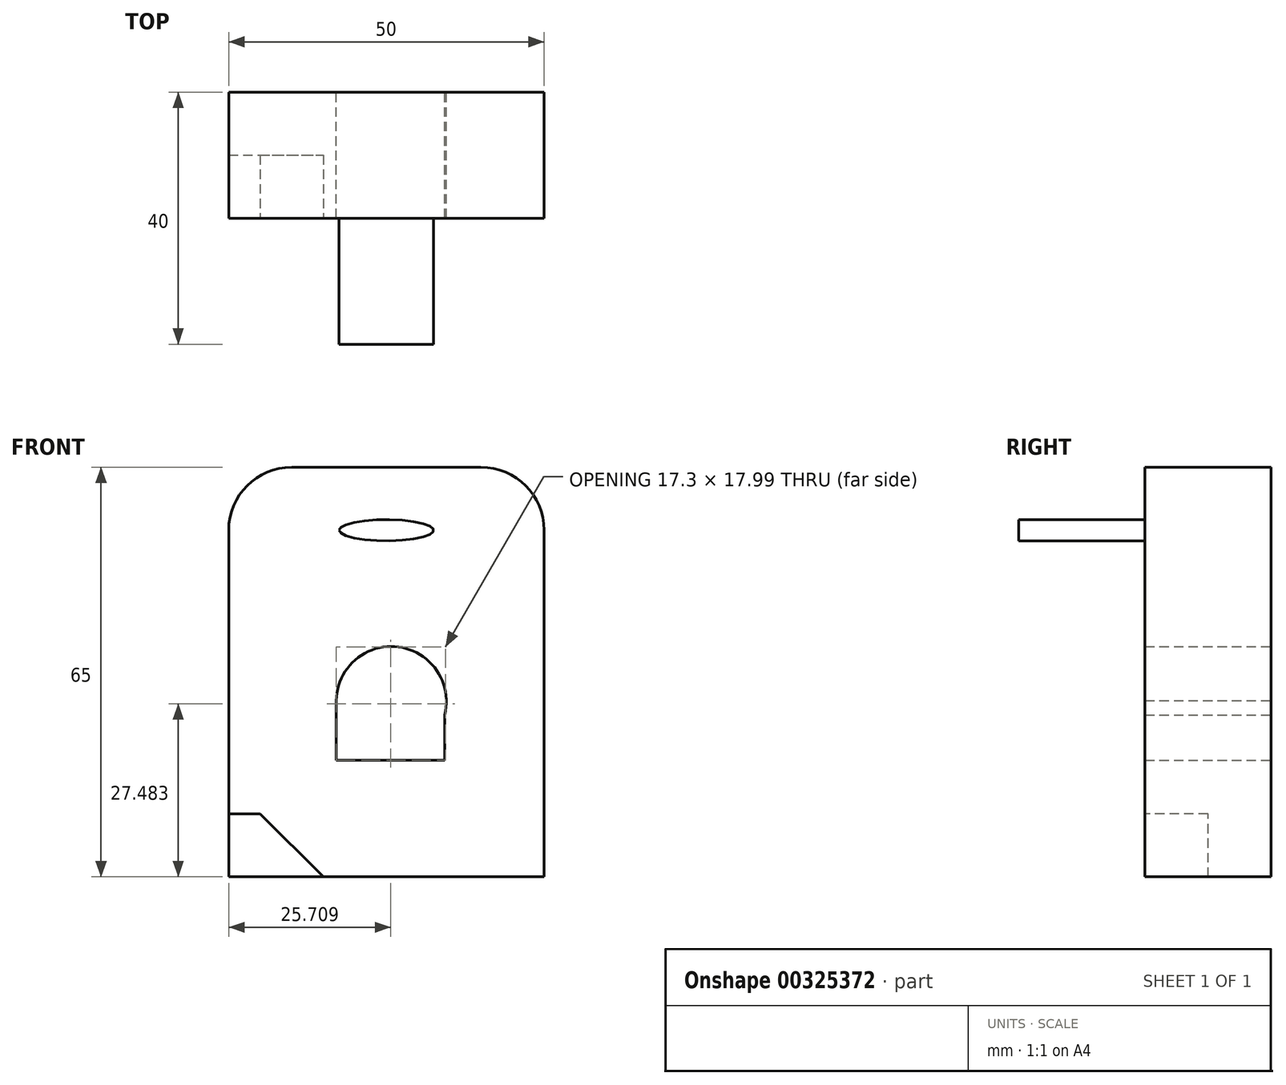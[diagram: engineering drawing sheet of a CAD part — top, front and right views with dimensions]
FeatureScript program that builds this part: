
annotation { "Feature Type Name" : "Feature", "Feature Type Description" : "" }
export const myFeature = defineFeature(function(context is Context, id is Id, definition is map)
    precondition{}
    {
        {
            var Q0;
            Q0=qCreatedBy(makeId("Front.planeOp"),FACE);
            var sketch = newSketch(context, id + "F0", { "sketchPlane" : qUnion([Q0])});
            skLineSegment(sketch, "E0.bottom", {"start": v(-25, -32.5) * mm, "end": v(25, -32.5) * mm});
            skLineSegment(sketch, "E0.top", {"start": v(-25, 32.5) * mm, "end": v(25, 32.5) * mm});
            skLineSegment(sketch, "E0.left", {"start": v(-25, -32.5) * mm, "end": v(-25, 32.5) * mm});
            skLineSegment(sketch, "E0.right", {"start": v(25, -32.5) * mm, "end": v(25, 32.5) * mm});
            skPoint(sketch, "E0.middle", {"position": v(0, 0) * mm});
            skSolve(sketch);
        }
        {
            var Q0;
            Q0=makeQuery(id+"F0.imprint","IMPRINT",FACE,{"disambiguationData":[TD([[makeQuery(id+"F0.imprint","IMPRINT",EDGE,{"derivedFrom":sQuery(id+"F0.wireOp",EDGE,"E0.bottom")}),1.0]])]});
            extrude(context, id + "F1", {"entities" : qUnion([Q0]), "depth" : 20 * mm});
        }
        {
            var Q0;
            Q0=makeQuery(id+"F1.opExtrude","CAP_FACE",FACE,{"disambiguationData":[OSD([sQuery(id+"F0.wireOp",EDGE,"E0.bottom"),sQuery(id+"F0.wireOp",EDGE,"E0.top"),sQuery(id+"F0.wireOp",EDGE,"E0.left"),sQuery(id+"F0.wireOp",EDGE,"E0.right")])],"isStart":false});
            var sketch = newSketch(context, id + "F2", { "sketchPlane" : qUnion([Q0])});
            skLineSegment(sketch, "E1", {"start": v(9.23, -14.01) * mm, "end": v(-7.94, -14.01) * mm});
            skLineSegment(sketch, "E2", {"start": v(-7.94, -14.01) * mm, "end": v(-7.94, -4.56) * mm});
            skLineSegment(sketch, "E3", {"start": v(-7.94, -4.56) * mm, "end": v(9.23, -4.56) * mm});
            skLineSegment(sketch, "E4", {"start": v(9.23, -4.56) * mm, "end": v(9.23, -14.01) * mm});
            skCircle(sketch, "E5", {"center": v(0.78, -4.67) * mm, "radius": 8.72 * mm});
            skCircle(sketch, "E6", {"center": v(-8.67, -44.04) * mm, "radius": 6.44 * mm, "construction": true});
            skSolve(sketch);
        }
        {
            var Q0;
            {var subQ0=sQuery(id+"F2.wireOp",EDGE,"E1");Q0=makeQuery(id+"F2.imprint","IMPRINT",FACE,{"disambiguationData":[TD([[makeQuery(id+"F2.imprint","IMPRINT",EDGE,{"derivedFrom":subQ0}),-1.0]])]});}
            var Q1;
            {var subQ0=sQuery(id+"F2.wireOp",EDGE,"E3");Q1=makeQuery(id+"F2.imprint","IMPRINT",FACE,{"disambiguationData":[TD([[makeQuery(id+"F2.imprint","IMPRINT",EDGE,{"derivedFrom":subQ0}),1.0]])]});}
            var Q2;
            {var subQ1=sQuery(id+"F2.wireOp",EDGE,"E3");Q2=makeQuery(id+"F2.imprint","IMPRINT",FACE,{"disambiguationData":[TD([[makeQuery(id+"F2.imprint","IMPRINT",EDGE,{"derivedFrom":subQ1}),-1.0]])]});}
            extrude(context, id + "F3", {"entities" : qUnion([Q0, Q1, Q2]), "operationType" : NewBodyOperationType.REMOVE, "depth" : 25.4 * mm, "hasSecondDirection" : true, "secondDirectionOppositeDirection" : true, "secondDirectionDepth" : 25.4 * mm});
        }
        {
            var Q0;
            Q0=makeQuery(id+"F1.opExtrude","SWEPT_EDGE",EDGE,{"disambiguationData":[OSD([sQuery(id+"F0.wireOp",EDGE,"E0.top"),sQuery(id+"F0.wireOp",EDGE,"E0.right")])]});
            var Q1;
            Q1=makeQuery(id+"F1.opExtrude","SWEPT_EDGE",EDGE,{"disambiguationData":[OSD([sQuery(id+"F0.wireOp",EDGE,"E0.top"),sQuery(id+"F0.wireOp",EDGE,"E0.left")])]});
            fillet(context, id + "F4", {"entities" : qUnion([Q0, Q1]), "radius" : 10 * mm, "tangentPropagation" : true, "allowEdgeOverflow" : false});
        }
        {
            var Q0;
            Q0=makeQuery(id+"F1.opExtrude","CAP_FACE",FACE,{"disambiguationData":[OSD([sQuery(id+"F0.wireOp",EDGE,"E0.bottom"),sQuery(id+"F0.wireOp",EDGE,"E0.top"),sQuery(id+"F0.wireOp",EDGE,"E0.left"),sQuery(id+"F0.wireOp",EDGE,"E0.right")])],"isStart":false});
            var sketch = newSketch(context, id + "F5", { "sketchPlane" : qUnion([Q0])});
            skLineSegment(sketch, "E7", {"start": v(-25, -22.5) * mm, "end": v(-20, -22.5) * mm});
            skLineSegment(sketch, "E8", {"start": v(-20, -22.5) * mm, "end": v(-10, -32.5) * mm});
            skLineSegment(sketch, "E9", {"start": v(-10, -32.5) * mm, "end": v(-25, -32.5) * mm});
            skLineSegment(sketch, "E10", {"start": v(-25, -32.5) * mm, "end": v(-25, -22.5) * mm});
            skSolve(sketch);
        }
        {
            var Q0;
            Q0=makeQuery(id+"F5.imprint","IMPRINT",FACE,{"disambiguationData":[TD([[makeQuery(id+"F5.imprint","IMPRINT",EDGE,{"derivedFrom":sQuery(id+"F5.wireOp",EDGE,"E7")}),-1.0]])]});
            extrude(context, id + "F6", {"entities" : qUnion([Q0]), "operationType" : NewBodyOperationType.REMOVE, "oppositeDirection" : true, "depth" : 10 * mm});
        }
        {
            var Q0;
            Q0=makeQuery(id+"F1.opExtrude","CAP_FACE",FACE,{"disambiguationData":[OSD([sQuery(id+"F0.wireOp",EDGE,"E0.bottom"),sQuery(id+"F0.wireOp",EDGE,"E0.top"),sQuery(id+"F0.wireOp",EDGE,"E0.left"),sQuery(id+"F0.wireOp",EDGE,"E0.right")])],"isStart":false});
            var sketch = newSketch(context, id + "F7", { "sketchPlane" : qUnion([Q0])});
            skEllipse(sketch, "E11", {"center": v(0, 22.5) * mm, "majorRadius": 7.5 * mm, "minorRadius": 1.68 * mm, "majorAxis": v(-1, 0)});
            skSolve(sketch);
        }
        {
            var Q0;
            Q0=makeQuery(id+"F7.imprint","IMPRINT",FACE,{"disambiguationData":[TD([[makeQuery(id+"F7.imprint","IMPRINT",EDGE,{"derivedFrom":sQuery(id+"F7.wireOp",EDGE,"E11")}),1.0]])]});
            extrude(context, id + "F8", {"entities" : qUnion([Q0]), "operationType" : NewBodyOperationType.ADD, "depth" : 20 * mm});
        }
        {
            var Q0;
            Q0=makeQuery(id+"F1.opExtrude","SWEPT_FACE",FACE,{"disambiguationData":[OSD([sQuery(id+"F0.wireOp",EDGE,"E0.bottom")])]});
            var sketch = newSketch(context, id + "F9", { "sketchPlane" : qUnion([Q0])});
            skCircle(sketch, "E12", {"center": v(25, 20) * mm, "radius": 5 * mm});
            skSolve(sketch);
        }
        {
            var Q0;
            {var subQ0=sQuery(id+"F9.wireOp",EDGE,"E12");var subQ1=sQuery(id+"F0.wireOp",EDGE,"E0.bottom");var subQ4=makeQuery(id+"F1.opExtrude","CAP_EDGE",EDGE,{"disambiguationData":[OSD([subQ1])],"isStart":false});var subQ5=makeQuery(id+"F9.imprint","INTERSECT",VERTEX,{"derivedFrom":[subQ4,subQ0]});Q0=makeQuery(id+"F9.imprint","IMPRINT",FACE,{"disambiguationData":[TD([[makeQuery(id+"F9.imprint","IMPRINT",EDGE,{"disambiguationData":[TD([[subQ5,1.0]])],"derivedFrom":subQ0}),1.0]])]});}
            extrude(context, id + "F10", {"entities" : qUnion([Q0]), "operationType" : NewBodyOperationType.REMOVE, "endBound" : BoundingType.THROUGH_ALL, "oppositeDirection" : true, "depth" : 20.03 * mm});
        }
    });
